# Revit family: RN 84238 Optiflex-Flowpress-Verschlusskappe
name_source: partatom
category: Rohrformteile
units: mm (PartAtom-declared; Revit-internal decimal feet)

## family parameters
Arbeitsebenenbasiert = Nein
Beim Laden mit Abzugskörper schneiden = Nein
Bemaßung runder Anschluss = Durchmesser verwenden
Gemeinsam genutzt = Nein
Immer vertikal = Ja
Teiletyp = Bogen

## types (6) — shared parameters
1.010.00.2 Blattnummer der Richtlinie = 29
1.010.00.3 Ausgabedatum (Monat) der Richtlinie = 201308
1.010.00.4 Herstellername = R. Nussbaum AG
1.010.00.5 Revisionsdatum der Datei = 20190521
1.010.00.6 Webadresse des Herstellers = http://www.nussbaum.ch
1.100.00.4 Produktbezeichnung = Versorgung
1.110.00.2 Index = 5
1.110.00.4 Produktbezeichnung = Optiflex
1.960/3L.00.8 Link (URL) = https://www.nussbaum.ch
29.700.00.4 Produktname = Optiflex-Flowpress-Verschlusskappe
29.700.00.5 Produktkennung = 2
29.700.00.6 Querschnittsform = 1
29.700.00.7 Nennweitensystem = DN
29.700.00.8 Nenndrucksystem = PN
29.710.02.4 Nenndruck = 10
29.710.02.5 max. zul. Überdruck [hPa] = 1000
29.710.02.7 max. zul. Dauer-Betriebsdruck [hPa] = 1000
29.710.02.9 max. zul. Dauer-Betriebstemperatur [°C] = 70
Connector Visibility = Nein
EnclosingSpace Visibility = Nein
Hersteller = R. Nussbaum AG
URL = https://www.nussbaum.ch

## per-type parameters (varying)
| type | 1.800.00.3 TGA-Nummer | 1.800.00.4 Kommentarfeld | 1.810.00.3 Hersteller-Bestellnummer | 1.810.00.4 DATANORM-Nummer | 1.810.00.6 GTIN-Nummer | 29.710.02.10 Formstück-Gewicht [kg] | 29.710.02.3 Benennung | CONNECTOR0_DIAMETER_dX_0r | CONNECTOR0_dX_01 | CONNECTOR0_ref_dX | Modell | R. Nussbaum AG 84238.21 de Visibility | R. Nussbaum AG 84238.22 de Visibility | R. Nussbaum AG 84238.23 de Visibility | R. Nussbaum AG 84238.24 de Visibility | R. Nussbaum AG 84238.25 de Visibility | R. Nussbaum AG 84238.26 de Visibility | Typenkommentare |
| DN=40 | 01900500000000000000000000000000000000000000000023000000000000000006 | 84238.26, Optiflex-Flowpress-Verschlusskappe, DN=40, L=62 | 84238.26 | 84238.26 | 7612945744920 | 0.445 | Optiflex-Flowpress-Verschlusskappe, DN=40, L=62 | 40 mm | 26 mm | 26 mm | 84238.26 | Nein | Nein | Nein | Nein | Nein | Ja | Optiflex-Flowpress-Verschlusskappe DN=40 |
| DN=32 | 01900500000000000000000000000000000000000000000023000000000000000005 | 84238.25, Optiflex-Flowpress-Verschlusskappe, DN=32, L=59 | 84238.25 | 84238.25 | 7612945731005 | 0.293 | Optiflex-Flowpress-Verschlusskappe, DN=32, L=59 | 32 mm | 26 mm | 26 mm | 84238.25 | Nein | Nein | Nein | Nein | Ja | Nein | Optiflex-Flowpress-Verschlusskappe DN=32 |
| DN=25 | 01900500000000000000000000000000000000000000000023000000000000000004 | 84238.24, Optiflex-Flowpress-Verschlusskappe, DN=25, L=44 | 84238.24 | 84238.24 | 7612945730992 | 0.152 | Optiflex-Flowpress-Verschlusskappe, DN=25, L=44 | 25 mm  [stored 0.082021 ft] | 20 mm | 20 mm | 84238.24 | Nein | Nein | Nein | Ja | Nein | Nein | Optiflex-Flowpress-Verschlusskappe DN=25 |
| DN=1 | 01900500000000000000000000000000000000000000000023000000000000000003 | 84238.23, Optiflex-Flowpress-Verschlusskappe, DN=25, L=41 | 84238.23 | 84238.23 | 7612945730985 | 0.087 | Optiflex-Flowpress-Verschlusskappe, DN=25, L=41 | 20 mm | 20 mm | 20 mm | 84238.23 | Nein | Nein | Ja | Nein | Nein | Nein | Optiflex-Flowpress-Verschlusskappe DN=25 |
| DN=15 | 01900500000000000000000000000000000000000000000023000000000000000002 | 84238.22, Optiflex-Flowpress-Verschlusskappe, DN=15, L=32 | 84238.22 | 84238.22 | 7612945730978 | 0.04 | Optiflex-Flowpress-Verschlusskappe, DN=15, L=32 | 15 mm | 14 mm  [stored 0.0459318 ft] | 14 mm  [stored 0.0459318 ft] | 84238.22 | Nein | Ja | Nein | Nein | Nein | Nein | Optiflex-Flowpress-Verschlusskappe DN=15 |
| DN=12 | 01900500000000000000000000000000000000000000000023000000000000000001 | 84238.21, Optiflex-Flowpress-Verschlusskappe, DN=12, L=30 | 84238.21 | 84238.21 | 7612945730961 | 0.026 | Optiflex-Flowpress-Verschlusskappe, DN=12, L=30 | 12 mm  [stored 0.0393701 ft] | 14 mm  [stored 0.0459318 ft] | 14 mm  [stored 0.0459318 ft] | 84238.21 | Ja | Nein | Nein | Nein | Nein | Nein | Optiflex-Flowpress-Verschlusskappe DN=12 |

note: [stored X ft] marks values corroborated as IEEE doubles in the binary element streams (Revit-internal decimal feet)

## geometry (parser evidence)
native form markers: Sweep x1
no freeform markers — native parametric forms only
